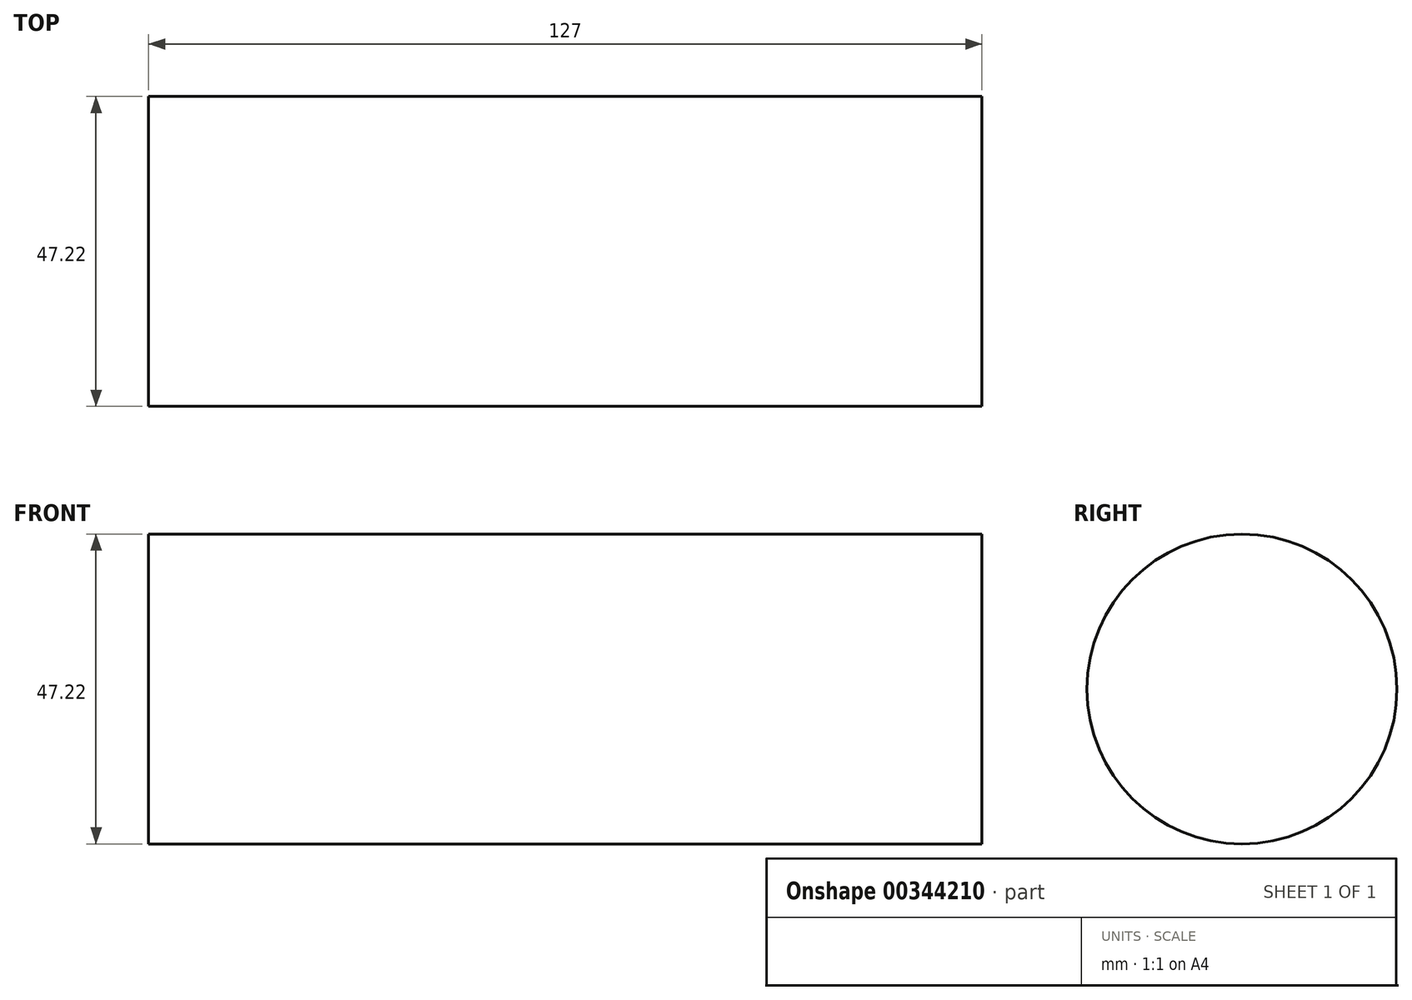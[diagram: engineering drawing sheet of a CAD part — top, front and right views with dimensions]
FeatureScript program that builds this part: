
annotation { "Feature Type Name" : "Feature", "Feature Type Description" : "" }
export const myFeature = defineFeature(function(context is Context, id is Id, definition is map)
    precondition{}
    {
        {
            var Q0;
            Q0=qCreatedBy(makeId("Right.planeOp"),FACE);
            var sketch = newSketch(context, id + "F0", { "sketchPlane" : qUnion([Q0])});
            skCircle(sketch, "E0", {"center": v(0, 30.58) * mm, "radius": 23.61 * mm});
            skSolve(sketch);
        }
        {
            var Q0;
            Q0=makeQuery(id+"F0.imprint","IMPRINT",FACE,{"disambiguationData":[TD([[makeQuery(id+"F0.imprint","IMPRINT",EDGE,{"derivedFrom":sQuery(id+"F0.wireOp",EDGE,"E0")}),1.0]])]});
            extrude(context, id + "F1", {"entities" : qUnion([Q0]), "depth" : 127 * mm});
        }
    });
